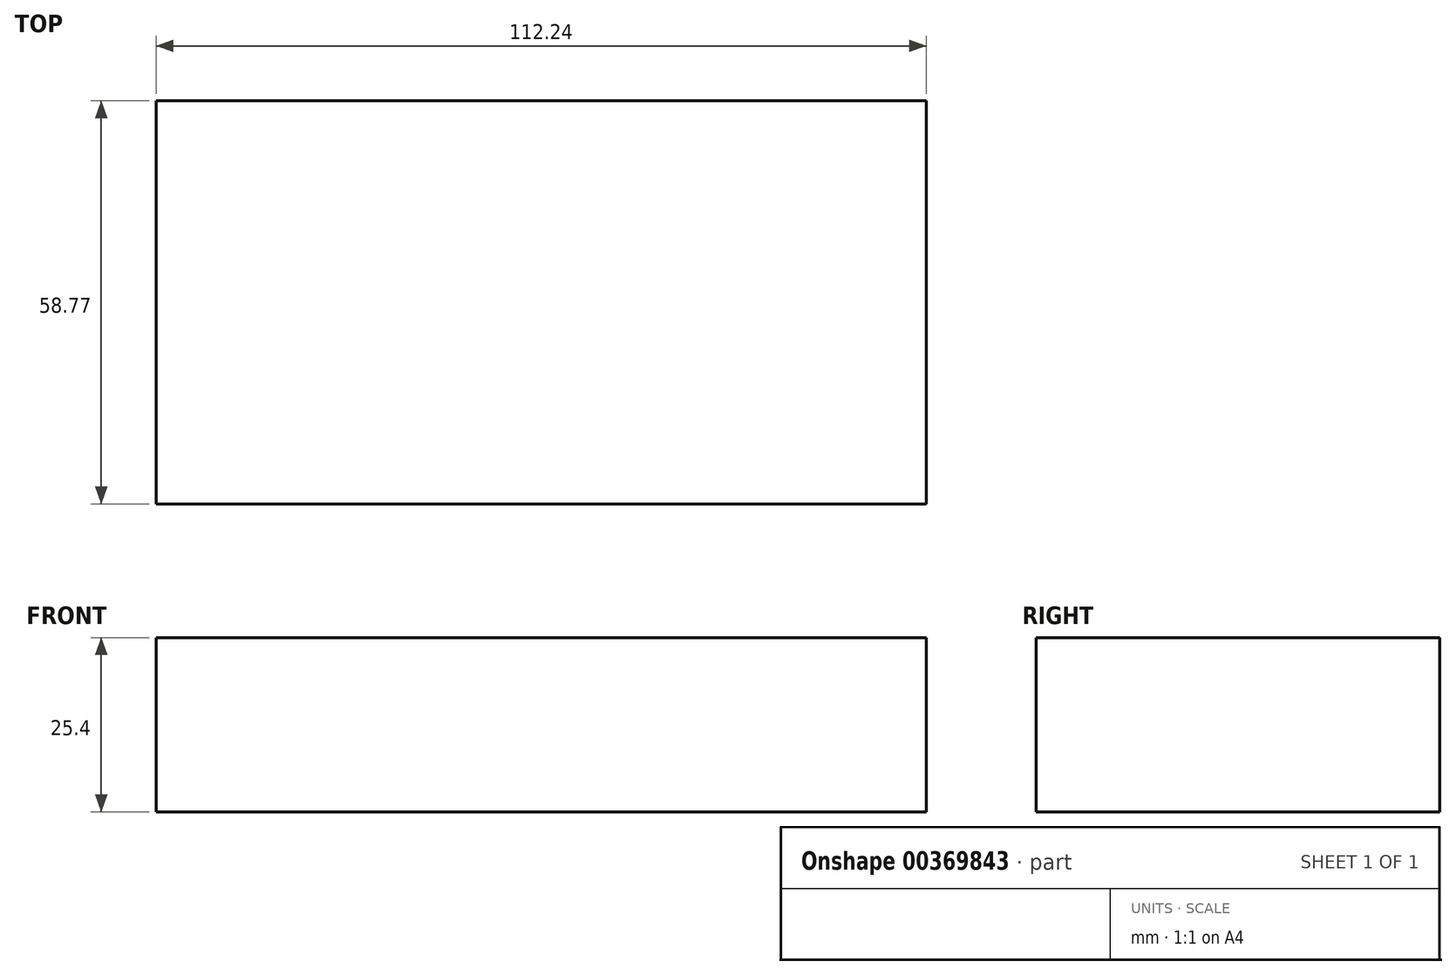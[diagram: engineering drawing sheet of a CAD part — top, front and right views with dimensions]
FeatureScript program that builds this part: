
annotation { "Feature Type Name" : "Feature", "Feature Type Description" : "" }
export const myFeature = defineFeature(function(context is Context, id is Id, definition is map)
    precondition{}
    {
        {
            var Q0;
            Q0=qCreatedBy(makeId("Top.planeOp"),FACE);
            var sketch = newSketch(context, id + "F0", { "sketchPlane" : qUnion([Q0])});
            skLineSegment(sketch, "E0.bottom", {"start": v(2.28, 0) * mm, "end": v(67.5, 0) * mm});
            skLineSegment(sketch, "E0.top", {"start": v(2.28, 44.37) * mm, "end": v(67.5, 44.37) * mm});
            skLineSegment(sketch, "E0.left", {"start": v(2.28, 0) * mm, "end": v(2.28, 44.37) * mm});
            skLineSegment(sketch, "E0.right", {"start": v(67.5, 0) * mm, "end": v(67.5, 44.37) * mm});
            skLineSegment(sketch, "E1.bottom", {"start": v(-56.12, -30.9) * mm, "end": v(56.12, -30.9) * mm});
            skLineSegment(sketch, "E1.top", {"start": v(-56.12, 27.87) * mm, "end": v(56.12, 27.87) * mm});
            skLineSegment(sketch, "E1.left", {"start": v(-56.12, -30.9) * mm, "end": v(-56.12, 27.87) * mm});
            skLineSegment(sketch, "E1.right", {"start": v(56.12, -30.9) * mm, "end": v(56.12, 27.87) * mm});
            skPoint(sketch, "E1.middle", {"position": v(0, -1.52) * mm});
            skLineSegment(sketch, "E2.bottom", {"start": v(7.58, 2.28) * mm, "end": v(-7.58, 2.28) * mm});
            skLineSegment(sketch, "E2.top", {"start": v(7.58, -5.3) * mm, "end": v(-7.58, -5.3) * mm});
            skLineSegment(sketch, "E2.left", {"start": v(7.58, 2.28) * mm, "end": v(7.58, -5.3) * mm});
            skLineSegment(sketch, "E2.right", {"start": v(-7.58, 2.28) * mm, "end": v(-7.58, -5.3) * mm});
            skSolve(sketch);
        }
        {
            var Q0;
            Q0=sQuery(id+"F0.wireOp",EDGE,"E1.right");
            var Q1;
            Q1=sQuery(id+"F0.wireOp",EDGE,"E1.bottom");
            var Q2;
            Q2=sQuery(id+"F0.wireOp",EDGE,"E1.left");
            var Q3;
            Q3=sQuery(id+"F0.wireOp",EDGE,"E1.top");
            extrude(context, id + "F1", {"bodyType" : ToolBodyType.SURFACE, "surfaceEntities" : qUnion([Q0, Q1, Q2, Q3]), "depth" : 25.4 * mm});
        }
    });
